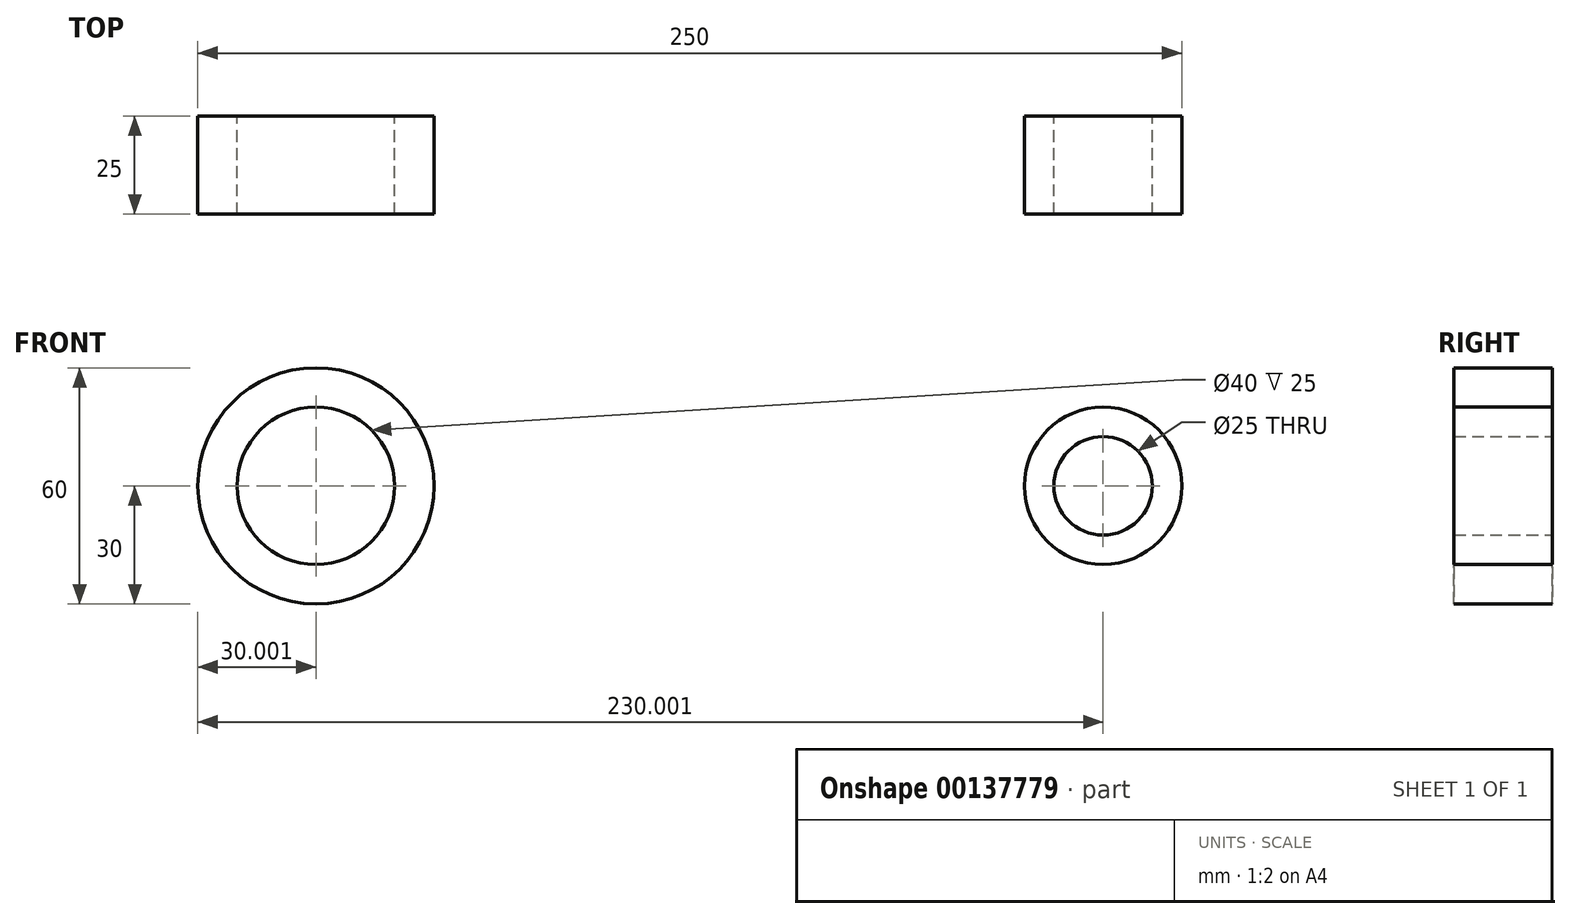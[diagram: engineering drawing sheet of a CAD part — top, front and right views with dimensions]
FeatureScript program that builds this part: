
annotation { "Feature Type Name" : "Feature", "Feature Type Description" : "" }
export const myFeature = defineFeature(function(context is Context, id is Id, definition is map)
    precondition{}
    {
        {
            var Q0;
            Q0=qCreatedBy(makeId("Front.planeOp"),FACE);
            var sketch = newSketch(context, id + "F0", { "sketchPlane" : qUnion([Q0])});
            skLineSegment(sketch, "E0", {"start": v(-116.68, 0) * mm, "end": v(138.8, 0) * mm, "construction": true});
            skCircle(sketch, "E1", {"center": v(-79.64, 0) * mm, "radius": 30 * mm});
            skCircle(sketch, "E2", {"center": v(120.36, 0) * mm, "radius": 20 * mm});
            skLineSegment(sketch, "E3", {"start": v(-77.9, 29.95) * mm, "end": v(121.36, 19.97) * mm});
            skLineSegment(sketch, "E4", {"start": v(-78.14, -29.96) * mm, "end": v(121.36, -19.97) * mm});
            skCircle(sketch, "E5", {"center": v(-79.64, 0) * mm, "radius": 20 * mm});
            skCircle(sketch, "E6", {"center": v(120.36, 0) * mm, "radius": 12.5 * mm});
            skSolve(sketch);
        }
        {
            var Q0;
            Q0=makeQuery(id+"F0.imprint","IMPRINT",FACE,{"disambiguationData":[TD([[makeQuery(id+"F0.imprint","IMPRINT",EDGE,{"derivedFrom":sQuery(id+"F0.wireOp",EDGE,"E5")}),-1.0]])]});
            var Q1;
            Q1=makeQuery(id+"F0.imprint","IMPRINT",FACE,{"disambiguationData":[TD([[makeQuery(id+"F0.imprint","IMPRINT",EDGE,{"derivedFrom":sQuery(id+"F0.wireOp",EDGE,"E6")}),-1.0]])]});
            extrude(context, id + "F1", {"entities" : qUnion([Q0, Q1]), "endBound" : BoundingType.SYMMETRIC, "depth" : 25 * mm});
        }
    });
